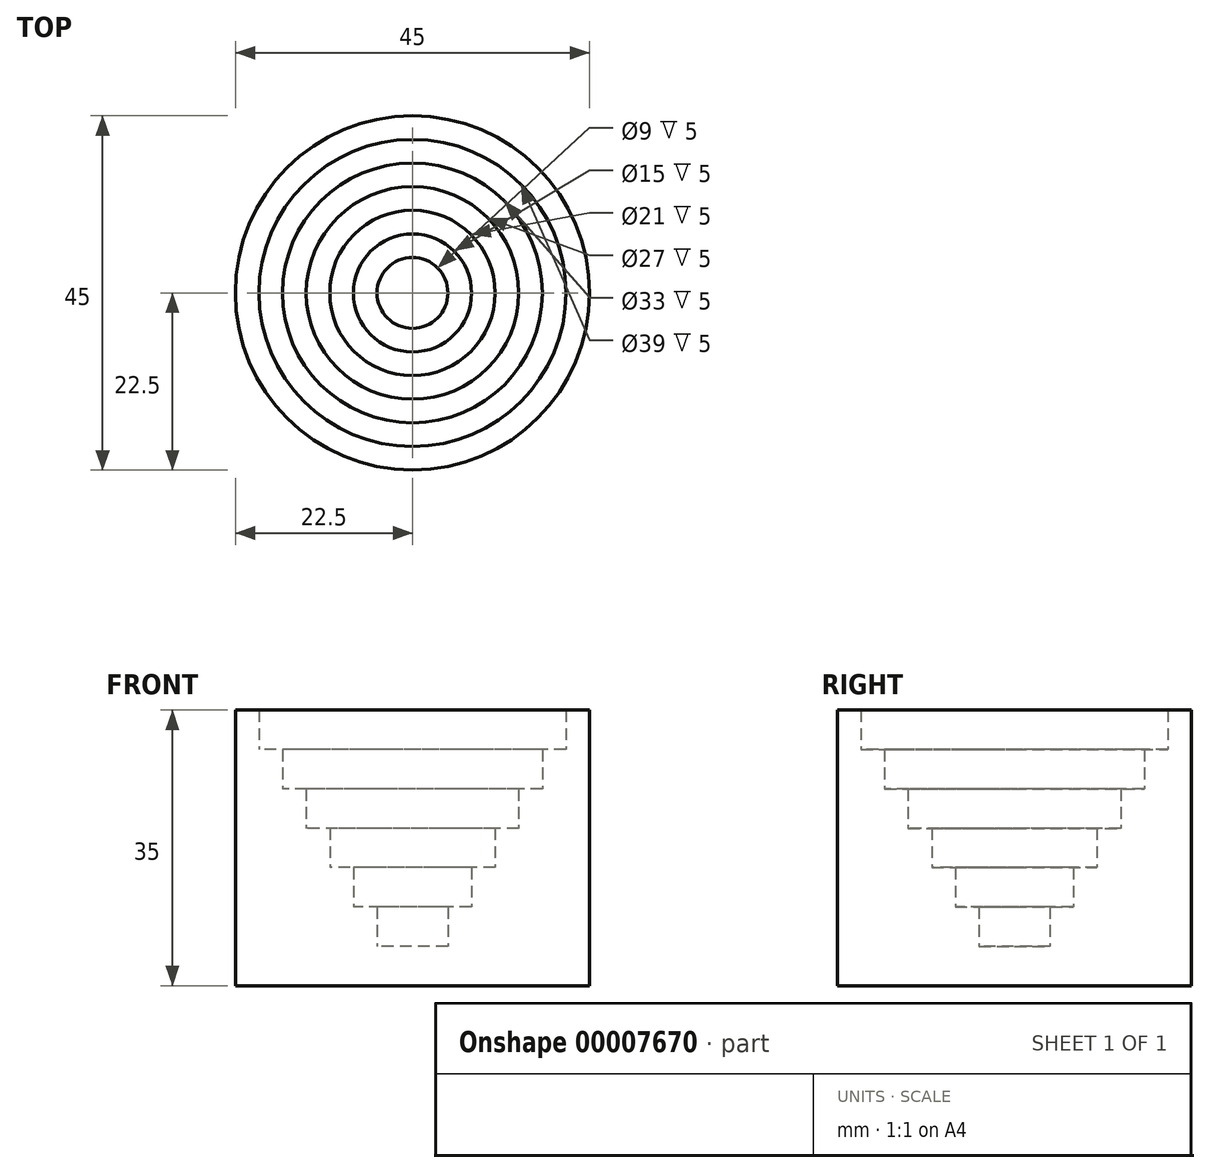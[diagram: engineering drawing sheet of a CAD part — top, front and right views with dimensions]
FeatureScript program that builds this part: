
annotation { "Feature Type Name" : "Feature", "Feature Type Description" : "" }
export const myFeature = defineFeature(function(context is Context, id is Id, definition is map)
    precondition{}
    {
        {
            var Q0;
            Q0=qCreatedBy(makeId("Top.planeOp"),FACE);
            var sketch = newSketch(context, id + "F0", { "sketchPlane" : qUnion([Q0])});
            skCircle(sketch, "E0", {"center": v(0, 0) * mm, "radius": 22.5 * mm});
            skCircle(sketch, "E1", {"center": v(0, 0) * mm, "radius": 4.5 * mm});
            skCircle(sketch, "E2", {"center": v(0, 0) * mm, "radius": 7.5 * mm});
            skCircle(sketch, "E3", {"center": v(0, 0) * mm, "radius": 10.5 * mm});
            skCircle(sketch, "E4", {"center": v(0, 0) * mm, "radius": 13.5 * mm});
            skCircle(sketch, "E5", {"center": v(0, 0) * mm, "radius": 16.5 * mm});
            skCircle(sketch, "E6", {"center": v(0, 0) * mm, "radius": 19.5 * mm});
            skSolve(sketch);
        }
        {
            var Q0;
            Q0=makeQuery(id+"F0.imprint","IMPRINT",FACE,{"disambiguationData":[TD([[makeQuery(id+"F0.imprint","IMPRINT",EDGE,{"derivedFrom":sQuery(id+"F0.wireOp",EDGE,"E1")}),1.0]])]});
            extrude(context, id + "F1", {"entities" : qUnion([Q0]), "depth" : 5 * mm});
        }
        {
            var Q0;
            Q0=makeQuery(id+"F0.imprint","IMPRINT",FACE,{"disambiguationData":[TD([[makeQuery(id+"F0.imprint","IMPRINT",EDGE,{"derivedFrom":sQuery(id+"F0.wireOp",EDGE,"E1")}),-1.0]])]});
            extrude(context, id + "F2", {"entities" : qUnion([Q0]), "operationType" : NewBodyOperationType.ADD, "depth" : 10 * mm});
        }
        {
            var Q0;
            Q0=makeQuery(id+"F0.imprint","IMPRINT",FACE,{"disambiguationData":[TD([[makeQuery(id+"F0.imprint","IMPRINT",EDGE,{"derivedFrom":sQuery(id+"F0.wireOp",EDGE,"E2")}),-1.0]])]});
            extrude(context, id + "F3", {"entities" : qUnion([Q0]), "operationType" : NewBodyOperationType.ADD, "depth" : 15 * mm});
        }
        {
            var Q0;
            Q0=makeQuery(id+"F0.imprint","IMPRINT",FACE,{"disambiguationData":[TD([[makeQuery(id+"F0.imprint","IMPRINT",EDGE,{"derivedFrom":sQuery(id+"F0.wireOp",EDGE,"E3")}),-1.0]])]});
            extrude(context, id + "F4", {"entities" : qUnion([Q0]), "operationType" : NewBodyOperationType.ADD, "depth" : 20 * mm});
        }
        {
            var Q0;
            Q0=makeQuery(id+"F0.imprint","IMPRINT",FACE,{"disambiguationData":[TD([[makeQuery(id+"F0.imprint","IMPRINT",EDGE,{"derivedFrom":sQuery(id+"F0.wireOp",EDGE,"E4")}),-1.0]])]});
            extrude(context, id + "F5", {"entities" : qUnion([Q0]), "operationType" : NewBodyOperationType.ADD, "depth" : 25 * mm});
        }
        {
            var Q0;
            Q0=makeQuery(id+"F0.imprint","IMPRINT",FACE,{"disambiguationData":[TD([[makeQuery(id+"F0.imprint","IMPRINT",EDGE,{"derivedFrom":sQuery(id+"F0.wireOp",EDGE,"E5")}),-1.0]])]});
            extrude(context, id + "F6", {"entities" : qUnion([Q0]), "operationType" : NewBodyOperationType.ADD, "depth" : 30 * mm});
        }
        {
            var Q0;
            Q0=makeQuery(id+"F0.imprint","IMPRINT",FACE,{"disambiguationData":[TD([[makeQuery(id+"F0.imprint","IMPRINT",EDGE,{"derivedFrom":sQuery(id+"F0.wireOp",EDGE,"E6")}),-1.0]])]});
            extrude(context, id + "F7", {"entities" : qUnion([Q0]), "operationType" : NewBodyOperationType.ADD, "depth" : 35 * mm});
        }
    });
